# Revit family: 49979003
name_source: partatom
category: Plumbing Fixtures
revit_build: Autodesk Revit 2018 (Build: 20170223_1515(x64)
units: mm (PartAtom-declared; Revit-internal decimal feet)

## family parameters
Always vertical = Yes
Cut with Voids When Loaded = No
OmniClass Number = 23.45.55.00
OmniClass Title = Sanitary Faucets, Wastes
Part Type = Normal
Room Calculation Point = No
Round Connector Dimension = Use Diameter
Shared = No
Work Plane-Based = No

## types (1)
- 49979003 Cover part for bath and shower faucet
    2D/3D/BIM Files URL = http://static.hansa.com
    3D View = https://static.hansa.com
    AssetType = Fixed
    BIMObjectName = 49979003
    BodyMaterial = Brass
    Brand = HANSA
    Catalog Drawing URL = http://static.hansa.com
    Category = Bathroom
    Certificate Global Mark = GM-WM-040199-I02-R00
    CloseOffRating = 0
    Color = Chrome
    Concealed Parts = Round rosette;Sleeve
    Dimension Drawing URL = http://static.hansa.com
    Diverter = Push operated diverter
    DurationUnit = Year
    EAN Number = 4057304012594
    EN Standard = EN 817
    ETIM Class Number = EC010546 Mechanical control system for shower
    FDV Document URL = http://www.hansa.com
    FaucetMainMaterial = Brass
    Features = Single-lever;Trim Kit
    Finish = Polished
    Flow Drawing URL = http://static.hansa.com
    FlowCoefficient = 0
    Group = Bath and shower faucet
    IfcExportAs = IfcValveType
    IfcExportType = FAUCET
    Installation Type = Concealed wall mounting
    Installation and Maintenance Guide URL = http://static.hansa.com
    Interactive AR View URL = https://static.hansa.com
    Lever Handle = Hot/Cold symbols;Single operating lever/handle
    Manufacturer = HANSA
    ManufacturerName = HANSA
    ManufacturerURL = http://www.hansa.com
    Market = International;Belgium;Netherlands;France;Czech Republic;Slovakia;Italy;Spain
    Material = Brass
    Max. Hot Water Supply = 80 °C
    Mobile Product Information URL = http://mpi.hansa.com
    Model = 49979003 Cover part for bath and shower faucet
    ModelReference = 49979003
    NBSDescription = Water supply fittings for baths
    NBSReference = 45-35-70/315
    Name = 49979003 Cover part for bath and shower faucet
    Name_en = 49979003 Cover part for bath and shower faucet
    Noise Class = II(ISO 3822)
    NominalDepth = 98 mm
    NominalHeight = 163 mm
    NominalWidth = 130 mm
    Product Code = 49979003
    Product Family = HANSAPRIMO
    Product Image URL = http://static.hansa.com
    Product URL = http://static.hansa.com
    Revision = 2
    Sales Package dimensions (LxWxH) = 210 x 165 x 60
    Shape = Sculptured
    Size = 130x100x165 mm
    Spare-Part Information URL = http://static.hansa.com
    Surface treatment = Chrome
    Technical DataSheet URL = http://www.hansa.com
    Temperature = Temperature limiter
    Temperature Adjustments = Limitation option for maximum temperature and flow-rate
    UNSPSC Class Number = 30181810 Faucet trim
    URL Declaration of Conformity = http://static.hansa.com
    URL Global Mark = http://static.hansa.com
    URL REACH = http://static.hansa.com
    Uniclass2 = Pr_40_30_96_07
    Uniclass2015Description = Bath manual water supply sets
    Uniclass2015Reference = Pr_40_20_87_07
    Version = 3
    VersionDate = 01/07/2022
    Warranty Information URL = http://warranty.hansa.com
    WarrantyDescription = http://warranty.hansa.com
    WarrantyDurationUnit = Year
    Working Pressure = 50 - 1000 kPa
    WorkingPressure = 50 - 1000 kPa

## geometry (parser evidence)
native form markers: Sweep x4
no freeform markers — native parametric forms only
